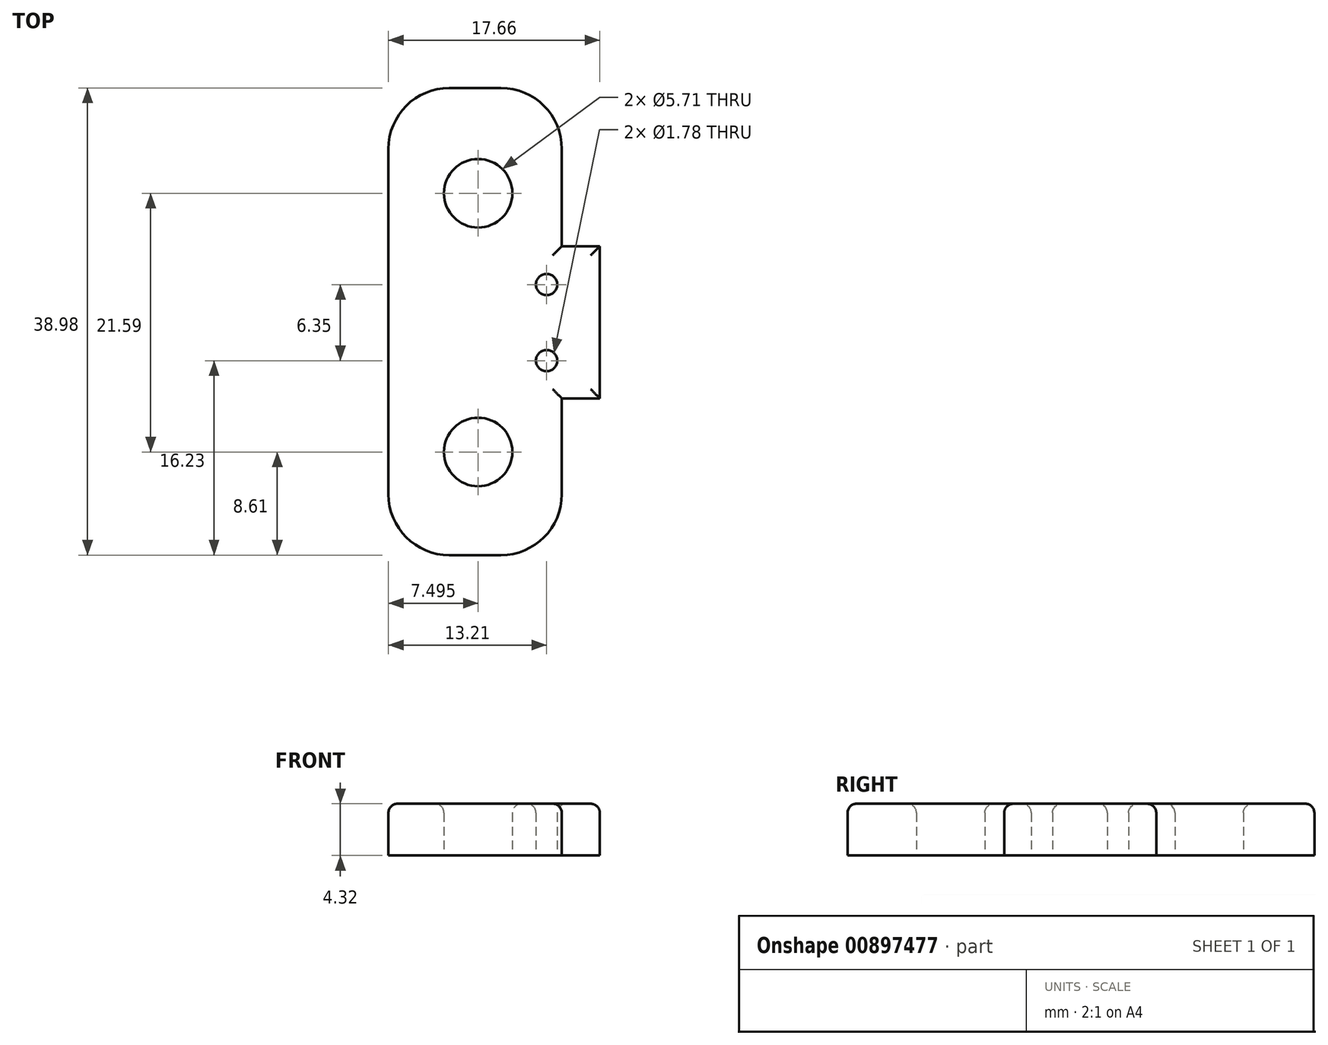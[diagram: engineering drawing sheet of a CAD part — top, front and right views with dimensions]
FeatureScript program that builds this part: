
annotation { "Feature Type Name" : "Feature", "Feature Type Description" : "" }
export const myFeature = defineFeature(function(context is Context, id is Id, definition is map)
    precondition{}
    {
        {
            var Q0;
            Q0=qCreatedBy(makeId("Top.planeOp"),FACE);
            var sketch = newSketch(context, id + "F0", { "sketchPlane" : qUnion([Q0])});
            skLineSegment(sketch, "E0", {"start": v(0, 0) * mm, "end": v(0, 63.5) * mm});
            skLineSegment(sketch, "E1", {"start": v(0, 63.5) * mm, "end": v(-41.91, 63.5) * mm});
            skLineSegment(sketch, "E2", {"start": v(-41.91, 63.5) * mm, "end": v(-41.91, 19) * mm});
            skLineSegment(sketch, "E3", {"start": v(-41.91, 19) * mm, "end": v(-41.91, 19) * mm});
            skLineSegment(sketch, "E4", {"start": v(-41.91, 19) * mm, "end": v(-41.91, 0) * mm});
            skCircle(sketch, "E5", {"center": v(-20.96, 42.74) * mm, "radius": 11.75 * mm});
            skCircle(sketch, "E6", {"center": v(-34.92, 9.5) * mm, "radius": 2.86 * mm});
            skLineSegment(sketch, "E7.top", {"start": v(-41.91, -20.7) * mm, "end": v(0, -20.7) * mm});
            skLineSegment(sketch, "E7.left", {"start": v(-41.91, 0) * mm, "end": v(-41.91, -20.7) * mm});
            skLineSegment(sketch, "E7.right", {"start": v(0, 0) * mm, "end": v(0, -20.7) * mm});
            skCircle(sketch, "E8", {"center": v(-34.92, -12.1) * mm, "radius": 2.86 * mm});
            skLineSegment(sketch, "E9", {"start": v(-41.91, 9.5) * mm, "end": v(-34.92, 9.5) * mm, "construction": true});
            skLineSegment(sketch, "E10", {"start": v(-20.96, 63.5) * mm, "end": v(-20.95, -20.7) * mm, "construction": true});
            skCircle(sketch, "E11", {"center": v(-36.83, 58.3) * mm, "radius": 1.9 * mm});
            skCircle(sketch, "E12", {"center": v(-5.08, 58.3) * mm, "radius": 1.9 * mm});
            skCircle(sketch, "E13", {"center": v(-5.08, 27.18) * mm, "radius": 1.9 * mm});
            skCircle(sketch, "E14", {"center": v(-36.83, 27.18) * mm, "radius": 1.9 * mm});
            skCircle(sketch, "E15", {"center": v(-6.99, -12.1) * mm, "radius": 2.86 * mm});
            skCircle(sketch, "E16", {"center": v(-6.99, 9.5) * mm, "radius": 2.86 * mm});
            skLineSegment(sketch, "E17", {"start": v(-36.83, 58.3) * mm, "end": v(-36.83, 27.18) * mm, "construction": true});
            skLineSegment(sketch, "E18", {"start": v(-36.83, 42.74) * mm, "end": v(-20.96, 42.74) * mm, "construction": true});
            skCircle(sketch, "E19", {"center": v(-1.27, 1.88) * mm, "radius": 0.89 * mm});
            skCircle(sketch, "E20", {"center": v(-1.27, -4.47) * mm, "radius": 0.89 * mm});
            skLineSegment(sketch, "E21", {"start": v(-6.99, 9.5) * mm, "end": v(-6.99, -12.1) * mm, "construction": true});
            skLineSegment(sketch, "E22", {"start": v(-1.27, 1.88) * mm, "end": v(-1.27, -4.47) * mm, "construction": true});
            skLineSegment(sketch, "E23", {"start": v(-1.27, -1.3) * mm, "end": v(-6.99, -1.3) * mm, "construction": true});
            skSolve(sketch);
        }
        {
            var Q0;
            Q0=makeQuery(id+"F0.imprint","IMPRINT",FACE,{"disambiguationData":[TD([[makeQuery(id+"F0.imprint","IMPRINT",EDGE,{"derivedFrom":sQuery(id+"F0.wireOp",EDGE,"E0")}),1.0]])]});
            var Q1;
            Q1=makeQuery(id+"F0.imprint","IMPRINT",FACE,{"disambiguationData":[TD([[makeQuery(id+"F0.imprint","IMPRINT",EDGE,{"derivedFrom":sQuery(id+"F0.wireOp",EDGE,"E7.bottom")}),-1.0]])]});
            extrude(context, id + "F1", {"entities" : qUnion([Q0, Q1]), "depth" : 4.32 * mm, "offsetDistance" : 25.4 * mm});
        }
        {
            var Q0;
            Q0=makeQuery(id+"F1.opExtrude","SWEPT_FACE",FACE,{"disambiguationData":[OSD([sQuery(id+"F0.wireOp",EDGE,"E0"),sQuery(id+"F0.wireOp",EDGE,"E7.right")])]});
            var sketch = newSketch(context, id + "F2", { "sketchPlane" : qUnion([Q0])});
            skLineSegment(sketch, "E24.bottom", {"start": v(-7.62, 4.32) * mm, "end": v(5.08, 4.32) * mm});
            skLineSegment(sketch, "E24.top", {"start": v(-7.62, 0) * mm, "end": v(5.08, 0) * mm});
            skLineSegment(sketch, "E24.left", {"start": v(-7.62, 4.32) * mm, "end": v(-7.62, 0) * mm});
            skLineSegment(sketch, "E24.right", {"start": v(5.08, 4.32) * mm, "end": v(5.08, 0) * mm});
            skSolve(sketch);
        }
        {
            var Q0;
            Q0=qSketchRegion(id+"F2",true);
            extrude(context, id + "F3", {"entities" : qUnion([Q0]), "operationType" : NewBodyOperationType.ADD, "depth" : 3.17 * mm, "offsetDistance" : 25.4 * mm});
        }
        {
            var Q0;
            Q0=makeQuery(id+"F1.opExtrude","SWEPT_EDGE",EDGE,{"disambiguationData":[OSD([sQuery(id+"F0.wireOp",EDGE,"E0"),sQuery(id+"F0.wireOp",EDGE,"jd0ScVzn-dBjU-jrx6-kBj3-BUJqmgKr12Eg")])]});
            var Q1;
            Q1=makeQuery(id+"F1.opExtrude","SWEPT_EDGE",EDGE,{"disambiguationData":[OSD([sQuery(id+"F0.wireOp",EDGE,"E4"),sQuery(id+"F0.wireOp",EDGE,"jd0ScVzn-dBjU-jrx6-kBj3-BUJqmgKr12Eg")])]});
            var Q2;
            Q2=makeQuery(id+"F1.opExtrude","SWEPT_EDGE",EDGE,{"disambiguationData":[OSD([sQuery(id+"F0.wireOp",EDGE,"E3"),sQuery(id+"F0.wireOp",EDGE,"E4")])]});
            var Q3;
            Q3=makeQuery(id+"F1.opExtrude","SWEPT_EDGE",EDGE,{"disambiguationData":[OSD([sQuery(id+"F0.wireOp",EDGE,"E2"),sQuery(id+"F0.wireOp",EDGE,"E3")])]});
            var Q4;
            Q4=makeQuery(id+"F1.opExtrude","SWEPT_EDGE",EDGE,{"disambiguationData":[OSD([sQuery(id+"F0.wireOp",EDGE,"E1"),sQuery(id+"F0.wireOp",EDGE,"E2")])]});
            var Q5;
            Q5=makeQuery(id+"F1.opExtrude","SWEPT_EDGE",EDGE,{"disambiguationData":[OSD([sQuery(id+"F0.wireOp",EDGE,"E0"),sQuery(id+"F0.wireOp",EDGE,"E1")])]});
            var Q6;
            Q6=makeQuery(id+"F1.opExtrude","SWEPT_EDGE",EDGE,{"disambiguationData":[OSD([sQuery(id+"F0.wireOp",EDGE,"E7.top"),sQuery(id+"F0.wireOp",EDGE,"E7.right")])]});
            var Q7;
            Q7=makeQuery(id+"F1.opExtrude","SWEPT_EDGE",EDGE,{"disambiguationData":[OSD([sQuery(id+"F0.wireOp",EDGE,"E7.top"),sQuery(id+"F0.wireOp",EDGE,"E7.left")])]});
            fillet(context, id + "F4", {"entities" : qUnion([Q0, Q1, Q2, Q3, Q4, Q5, Q6, Q7]), "radius" : 5.08 * mm, "tangentPropagation" : true, "defaultsChanged" : false, "vertexSettings" : [], "allowEdgeOverflow" : false});
        }
        {
            var Q0;
            Q0=makeQuery(id+"F3.boolean.opBoolean","MERGE",FACE,{"derivedFrom":[makeQuery(id+"F1.opExtrude","CAP_FACE",FACE,{"disambiguationData":[OSD([sQuery(id+"F0.wireOp",EDGE,"E0"),sQuery(id+"F0.wireOp",EDGE,"E1"),sQuery(id+"F0.wireOp",EDGE,"E2"),sQuery(id+"F0.wireOp",EDGE,"E4"),sQuery(id+"F0.wireOp",EDGE,"E5"),sQuery(id+"F0.wireOp",EDGE,"E6"),sQuery(id+"F0.wireOp",EDGE,"E7.top"),sQuery(id+"F0.wireOp",EDGE,"E7.left"),sQuery(id+"F0.wireOp",EDGE,"E7.right"),sQuery(id+"F0.wireOp",EDGE,"E8"),sQuery(id+"F0.wireOp",EDGE,"E11"),sQuery(id+"F0.wireOp",EDGE,"E12"),sQuery(id+"F0.wireOp",EDGE,"E13"),sQuery(id+"F0.wireOp",EDGE,"E14"),sQuery(id+"F0.wireOp",EDGE,"E15"),sQuery(id+"F0.wireOp",EDGE,"E16"),sQuery(id+"F0.wireOp",EDGE,"E19"),sQuery(id+"F0.wireOp",EDGE,"E20")])],"isStart":false}),makeQuery(id+"F3.opExtrude","SWEPT_FACE",FACE,{"disambiguationData":[OSD([sQuery(id+"F2.wireOp",EDGE,"E24.bottom")])]})]});
            var sketch = newSketch(context, id + "F5", { "sketchPlane" : qUnion([Q0])});
            skLineSegment(sketch, "E25", {"start": v(-14.48, -25.96) * mm, "end": v(-14.48, 18.28) * mm});
            skLineSegment(sketch, "E26", {"start": v(-14.48, 18.28) * mm, "end": v(4.94, 18.28) * mm});
            skLineSegment(sketch, "E27", {"start": v(4.94, 18.28) * mm, "end": v(4.94, 69.24) * mm});
            skLineSegment(sketch, "E28", {"start": v(4.94, 69.24) * mm, "end": v(-51.07, 69.24) * mm});
            skLineSegment(sketch, "E29", {"start": v(-51.07, 69.24) * mm, "end": v(-51.07, -23.48) * mm});
            skLineSegment(sketch, "E30", {"start": v(-51.07, -23.48) * mm, "end": v(-14.48, -25.96) * mm});
            skSolve(sketch);
        }
        {
            var Q0;
            Q0 = qSketchRegion(id + "F5", true);
            extrude(context, id + "F6", {"entities" : qUnion([Q0]), "operationType" : NewBodyOperationType.REMOVE, "oppositeDirection" : true, "depth" : 25.4 * mm, "offsetDistance" : 25.4 * mm});
        }
        {
            var Q0;
            Q0=makeQuery(id+"F6.boolean.opBoolean","INTERSECT",EDGE,{"derivedFrom":[makeQuery(id+"F1.opExtrude","SWEPT_FACE",FACE,{"disambiguationData":[OSD([sQuery(id+"F0.wireOp",EDGE,"E7.top")])]}),makeQuery(id+"F6.opExtrude","SWEPT_FACE",FACE,{"disambiguationData":[OSD([sQuery(id+"F5.wireOp",EDGE,"E25")])]})]});
            var Q1;
            Q1=makeQuery(id+"F6.boolean.opBoolean","COPY",EDGE,{"derivedFrom":makeQuery(id+"F6.opExtrude","SWEPT_EDGE",EDGE,{"disambiguationData":[OSD([sQuery(id+"F5.wireOp",EDGE,"E25"),sQuery(id+"F5.wireOp",EDGE,"E26")])]})});
            var Q2;
            {var subQ9=sQuery(id+"F0.wireOp",EDGE,"E7.right");var subQ16=sQuery(id+"F0.wireOp",EDGE,"E1");var subQ17=sQuery(id+"F0.wireOp",EDGE,"E0");Q2=makeQuery(id+"F6.boolean.opBoolean","INTERSECT",EDGE,{"derivedFrom":[makeQuery(id+"F3.boolean.opBoolean","SPLIT",FACE,{"disambiguationData":[TD([makeQuery(id+"F1.opExtrude","SWEPT_FACE",FACE,{"disambiguationData":[OSD([subQ16])]})])],"derivedFrom":makeQuery(id+"F1.opExtrude","SWEPT_FACE",FACE,{"disambiguationData":[OSD([subQ17,subQ9])]})}),makeQuery(id+"F6.opExtrude","SWEPT_FACE",FACE,{"disambiguationData":[OSD([sQuery(id+"F5.wireOp",EDGE,"E26")])]})]});}
            fillet(context, id + "F7", {"entities" : qUnion([Q0, Q1, Q2]), "tangentPropagation" : true, "radius" : 5.08 * mm, "defaultsChanged" : false, "vertexSettings" : [], "allowEdgeOverflow" : false});
        }
        {
            var Q0;
            Q0=makeQuery(id+"F3.boolean.opBoolean","MERGE",FACE,{"derivedFrom":[makeQuery(id+"F1.opExtrude","CAP_FACE",FACE,{"disambiguationData":[OSD([sQuery(id+"F0.wireOp",EDGE,"E0"),sQuery(id+"F0.wireOp",EDGE,"E1"),sQuery(id+"F0.wireOp",EDGE,"E2"),sQuery(id+"F0.wireOp",EDGE,"E4"),sQuery(id+"F0.wireOp",EDGE,"E5"),sQuery(id+"F0.wireOp",EDGE,"E6"),sQuery(id+"F0.wireOp",EDGE,"E7.top"),sQuery(id+"F0.wireOp",EDGE,"E7.left"),sQuery(id+"F0.wireOp",EDGE,"E7.right"),sQuery(id+"F0.wireOp",EDGE,"E8"),sQuery(id+"F0.wireOp",EDGE,"E11"),sQuery(id+"F0.wireOp",EDGE,"E12"),sQuery(id+"F0.wireOp",EDGE,"E13"),sQuery(id+"F0.wireOp",EDGE,"E14"),sQuery(id+"F0.wireOp",EDGE,"E15"),sQuery(id+"F0.wireOp",EDGE,"E16"),sQuery(id+"F0.wireOp",EDGE,"E19"),sQuery(id+"F0.wireOp",EDGE,"E20")])],"isStart":false}),makeQuery(id+"F3.opExtrude","SWEPT_FACE",FACE,{"disambiguationData":[OSD([sQuery(id+"F2.wireOp",EDGE,"E24.bottom")])]})]});
            fillet(context, id + "F8", {"entities" : qUnion([Q0]), "tangentPropagation" : true, "radius" : 0.76 * mm, "defaultsChanged" : true, "vertexSettings" : [], "allowEdgeOverflow" : false});
        }
    });
